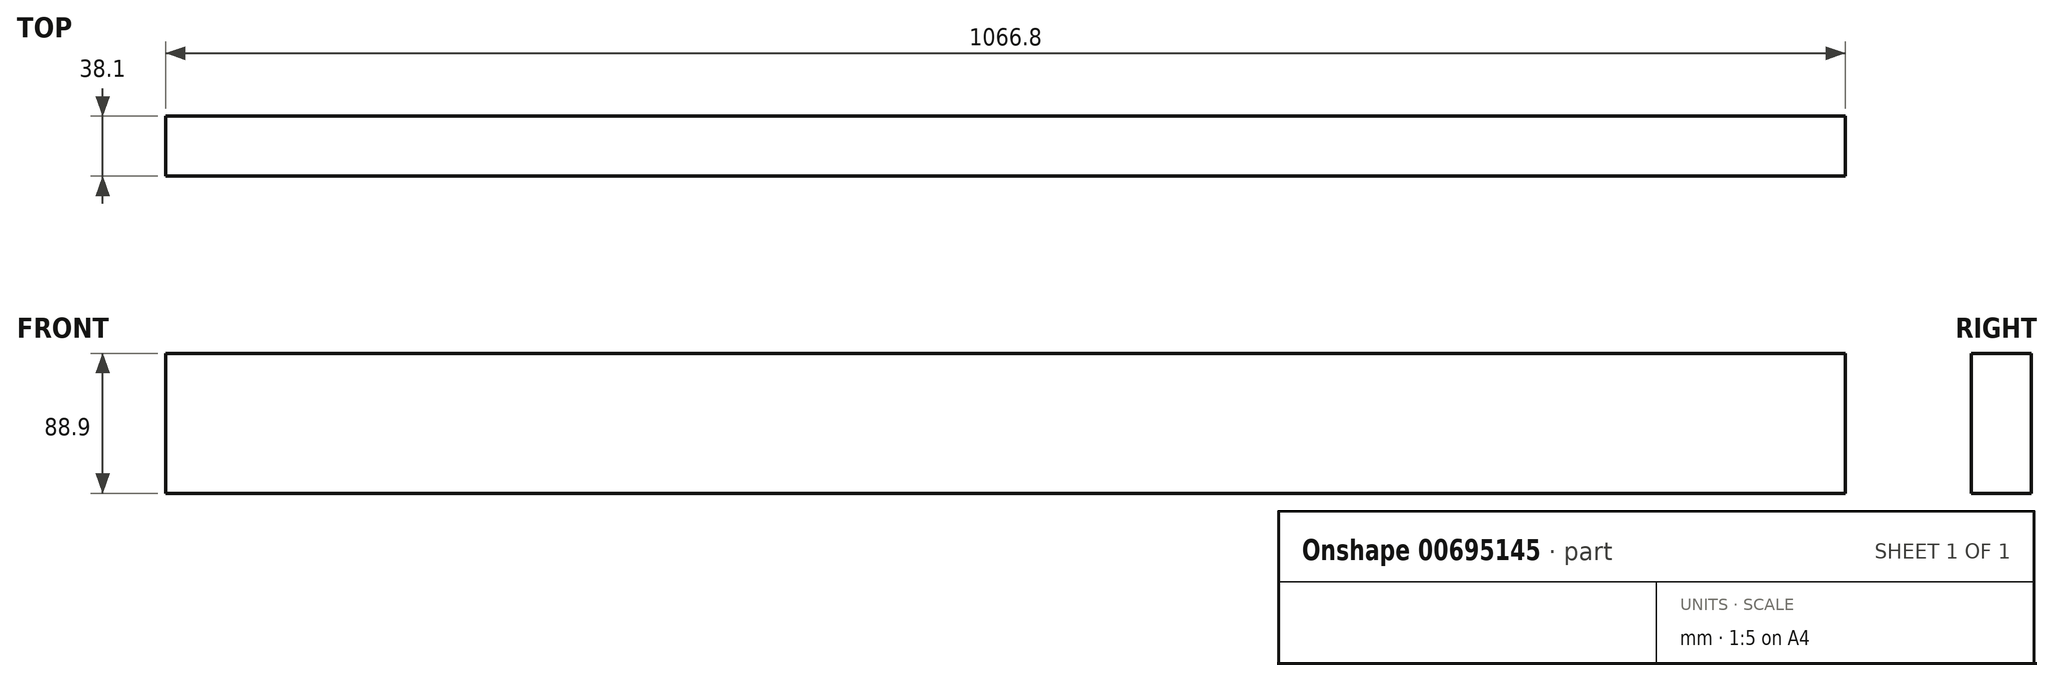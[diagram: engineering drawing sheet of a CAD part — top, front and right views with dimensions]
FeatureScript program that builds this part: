
annotation { "Feature Type Name" : "Feature", "Feature Type Description" : "" }
export const myFeature = defineFeature(function(context is Context, id is Id, definition is map)
    precondition{}
    {
        {
            var Q0;
            Q0=qCreatedBy(makeId("Right.planeOp"),FACE);
            var sketch = newSketch(context, id + "F0", { "sketchPlane" : qUnion([Q0])});
            skLineSegment(sketch, "E0.bottom", {"start": v(3952.9, 478.6) * mm, "end": v(3991, 478.6) * mm});
            skLineSegment(sketch, "E0.top", {"start": v(3952.9, 389.7) * mm, "end": v(3991, 389.7) * mm});
            skLineSegment(sketch, "E0.left", {"start": v(3952.9, 478.6) * mm, "end": v(3952.9, 389.7) * mm});
            skLineSegment(sketch, "E0.right", {"start": v(3991, 478.6) * mm, "end": v(3991, 389.7) * mm});
            skSolve(sketch);
        }
        {
            var Q0;
            Q0=makeQuery(id+"F0.imprint","IMPRINT",FACE,{"disambiguationData":[TD([[makeQuery(id+"F0.imprint","IMPRINT",EDGE,{"derivedFrom":sQuery(id+"F0.wireOp",EDGE,"E0.bottom")}),-1.0]])]});
            extrude(context, id + "F1", {"entities" : qUnion([Q0]), "depth" : 1066.8 * mm, "offsetDistance" : 25.4 * mm});
        }
    });
